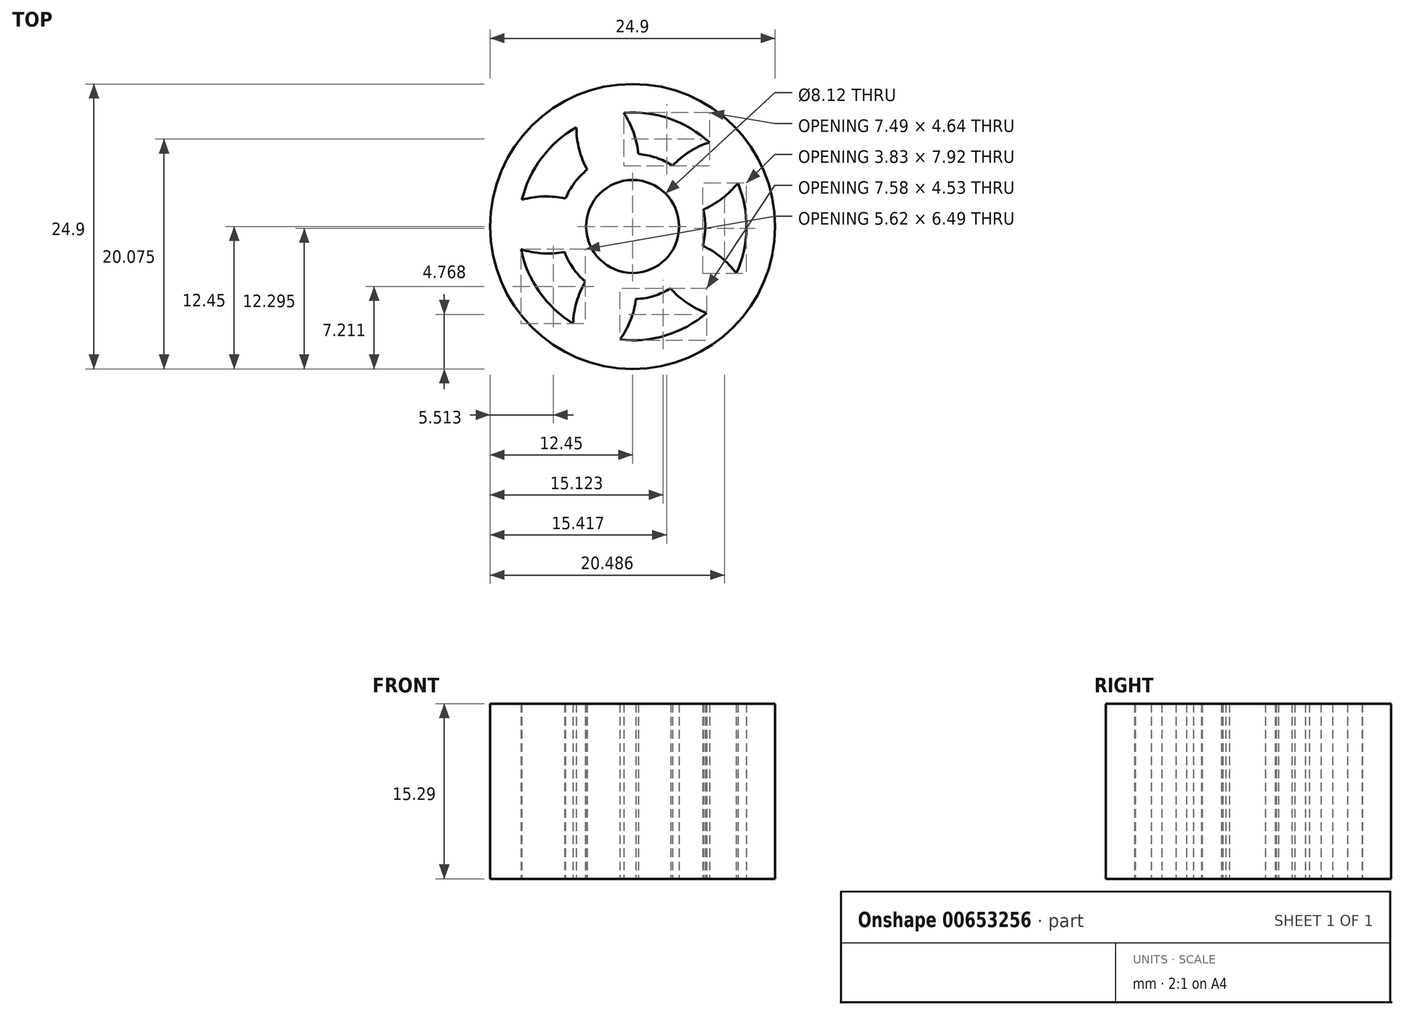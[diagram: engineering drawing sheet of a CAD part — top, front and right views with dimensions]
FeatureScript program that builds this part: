
annotation { "Feature Type Name" : "Feature", "Feature Type Description" : "" }
export const myFeature = defineFeature(function(context is Context, id is Id, definition is map)
    precondition{}
    {
        {
            var Q0;
            Q0=qCreatedBy(makeId("Top.planeOp"),FACE);
            var sketch = newSketch(context, id + "F0", { "sketchPlane" : qUnion([Q0])});
            skCircle(sketch, "E0", {"center": v(0, 0) * mm, "radius": 12.45 * mm});
            skCircle(sketch, "E1", {"center": v(0, 0) * mm, "radius": 4.06 * mm});
            skArc(sketch, "E2", {"start": v(-4.9, 8.65) * mm, "mid": v(-7.95, 5.98) * mm, "end": v(-9.67, 2.32) * mm});
            skArc(sketch, "E3", {"start": v(-3.96, 4.96) * mm, "mid": v(-5.08, 3.82) * mm, "end": v(-5.87, 2.43) * mm});
            skArc(sketch, "E4", {"start": v(-5.87, 2.43) * mm, "mid": v(-7.78, 2.62) * mm, "end": v(-9.67, 2.32) * mm});
            skArc(sketch, "E5", {"start": v(-4.9, 8.65) * mm, "mid": v(-4.67, 6.75) * mm, "end": v(-3.96, 4.96) * mm});
            skArc(sketch, "E6.1.0", {"start": v(-9.75, -2) * mm, "mid": v(-7.86, -2.36) * mm, "end": v(-5.94, -2.24) * mm});
            skArc(sketch, "E6.1.1", {"start": v(-9.75, -2) * mm, "mid": v(-8.15, -5.71) * mm, "end": v(-5.2, -8.48) * mm});
            skArc(sketch, "E6.1.2", {"start": v(-4.13, -4.83) * mm, "mid": v(-4.9, -6.59) * mm, "end": v(-5.2, -8.48) * mm});
            skArc(sketch, "E6.1.3", {"start": v(-5.94, -2.24) * mm, "mid": v(-5.2, -3.65) * mm, "end": v(-4.13, -4.83) * mm});
            skArc(sketch, "E6.2.0", {"start": v(-1.11, -9.89) * mm, "mid": v(-0.19, -8.2) * mm, "end": v(0.3, -6.34) * mm});
            skArc(sketch, "E6.2.1", {"start": v(-1.11, -9.89) * mm, "mid": v(2.91, -9.51) * mm, "end": v(6.46, -7.57) * mm});
            skArc(sketch, "E6.2.2", {"start": v(3.32, -5.42) * mm, "mid": v(4.75, -6.69) * mm, "end": v(6.46, -7.57) * mm});
            skArc(sketch, "E6.2.3", {"start": v(0.3, -6.34) * mm, "mid": v(1.86, -6.07) * mm, "end": v(3.32, -5.42) * mm});
            skArc(sketch, "E7.3.3.0", {"start": v(9.06, -4.12) * mm, "mid": v(7.74, -2.71) * mm, "end": v(6.12, -1.68) * mm});
            skArc(sketch, "E7.4.3.0", {"start": v(9.06, -4.12) * mm, "mid": v(9.95, -0.17) * mm, "end": v(9.2, 3.8) * mm});
            skArc(sketch, "E7.8.3.0", {"start": v(6.17, 1.48) * mm, "mid": v(7.83, 2.45) * mm, "end": v(9.2, 3.8) * mm});
            skArc(sketch, "E7.12.3.0", {"start": v(6.12, -1.68) * mm, "mid": v(6.35, -0.1) * mm, "end": v(6.17, 1.48) * mm});
            skArc(sketch, "E7.3.4.0", {"start": v(6.71, 7.34) * mm, "mid": v(4.97, 6.53) * mm, "end": v(3.5, 5.3) * mm});
            skArc(sketch, "E7.4.4.0", {"start": v(6.71, 7.34) * mm, "mid": v(3.23, 9.4) * mm, "end": v(-0.78, 9.92) * mm});
            skArc(sketch, "E7.8.4.0", {"start": v(0.5, 6.33) * mm, "mid": v(0.09, 8.2) * mm, "end": v(-0.78, 9.92) * mm});
            skArc(sketch, "E7.12.4.0", {"start": v(3.5, 5.3) * mm, "mid": v(2.06, 6) * mm, "end": v(0.5, 6.33) * mm});
            skSolve(sketch);
        }
        {
            var Q0;
            Q0=makeQuery(id+"F0.imprint","IMPRINT",FACE,{"disambiguationData":[TD([[makeQuery(id+"F0.imprint","IMPRINT",EDGE,{"derivedFrom":sQuery(id+"F0.wireOp",EDGE,"E0")}),1.0]])]});
            extrude(context, id + "F1", {"entities" : qUnion([Q0]), "depth" : 15.29 * mm, "offsetDistance" : 25 * mm});
        }
    });
